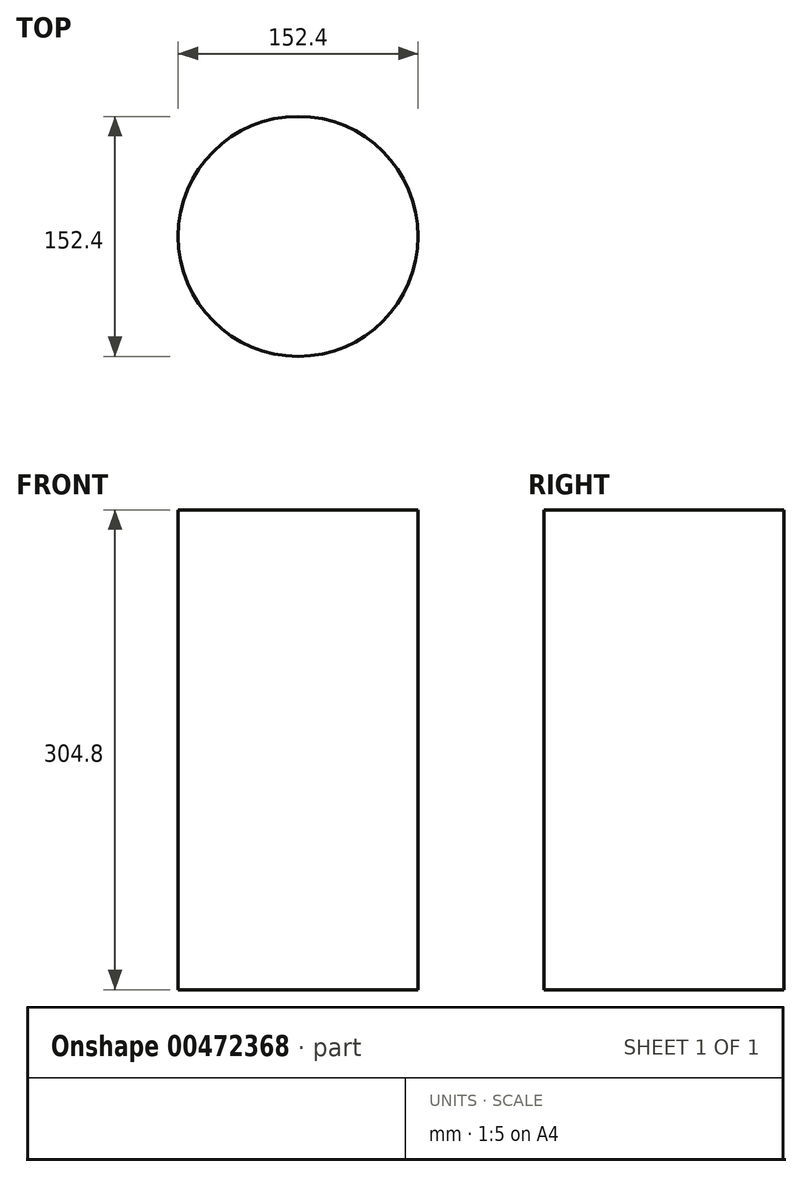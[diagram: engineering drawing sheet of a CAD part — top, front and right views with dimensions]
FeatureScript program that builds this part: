
annotation { "Feature Type Name" : "Feature", "Feature Type Description" : "" }
export const myFeature = defineFeature(function(context is Context, id is Id, definition is map)
    precondition{}
    {
        {
            var Q0;
            Q0=qCreatedBy(makeId("Top.planeOp"),FACE);
            var sketch = newSketch(context, id + "F0", { "sketchPlane" : qUnion([Q0])});
            skCircle(sketch, "E0", {"center": v(0, 0) * mm, "radius": 76.2 * mm});
            skSolve(sketch);
        }
        {
            var Q0;
            Q0=qSketchRegion(id+"F0",true);
            extrude(context, id + "F1", {"entities" : qUnion([Q0]), "depth" : 304.8 * mm});
        }
    });
